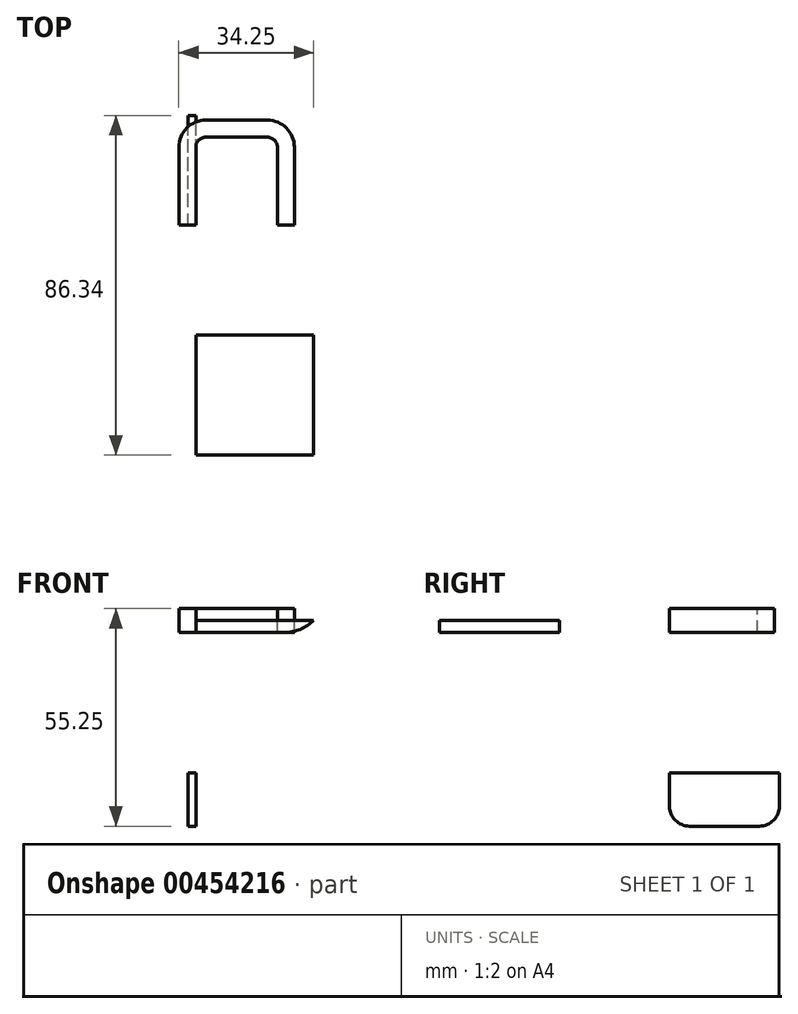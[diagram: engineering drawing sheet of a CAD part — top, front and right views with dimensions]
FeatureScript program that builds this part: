
annotation { "Feature Type Name" : "Feature", "Feature Type Description" : "" }
export const myFeature = defineFeature(function(context is Context, id is Id, definition is map)
    precondition{}
    {
        {
            var Q0;
            Q0=qCreatedBy(makeId("Top.planeOp"),FACE);
            var sketch = newSketch(context, id + "F0", { "sketchPlane" : qUnion([Q0])});
            skLineSegment(sketch, "E0", {"start": v(0, 0) * mm, "end": v(0, 19.84) * mm});
            skLineSegment(sketch, "E1", {"start": v(2.54, 22.38) * mm, "end": v(18.18, 22.38) * mm});
            skLineSegment(sketch, "E2", {"start": v(20.72, 19.84) * mm, "end": v(20.72, 0) * mm});
            skPoint(sketch, "E3.visualSharp", {"position": v(0, 22.38) * mm});
            skArc(sketch, "E3.filletArc", {"start": v(2.54, 22.38) * mm, "mid": v(0.74, 21.64) * mm, "end": v(0, 19.84) * mm});
            skPoint(sketch, "E4.visualSharp", {"position": v(20.72, 22.38) * mm});
            skArc(sketch, "E4.filletArc", {"start": v(20.72, 19.84) * mm, "mid": v(19.98, 21.64) * mm, "end": v(18.18, 22.38) * mm});
            skSolve(sketch);
        }
        {
            var Q0;
            Q0=qCreatedBy(makeId("Front.planeOp"),FACE);
            var sketch = newSketch(context, id + "F1", { "sketchPlane" : qUnion([Q0])});
            skLineSegment(sketch, "E5.bottom", {"start": v(0, 0) * mm, "end": v(-4.32, 0) * mm});
            skLineSegment(sketch, "E5.top", {"start": v(0, 6.04) * mm, "end": v(-4.32, 6.04) * mm});
            skLineSegment(sketch, "E5.left", {"start": v(0, 0) * mm, "end": v(0, 6.04) * mm});
            skLineSegment(sketch, "E5.right", {"start": v(-4.32, 0) * mm, "end": v(-4.32, 6.04) * mm});
            skSolve(sketch);
        }
        {
            var Q0;
            Q0=makeQuery(id+"F1.imprint","IMPRINT",FACE,{"disambiguationData":[TD([[makeQuery(id+"F1.imprint","IMPRINT",EDGE,{"derivedFrom":sQuery(id+"F1.wireOp",EDGE,"E5.bottom")}),-1.0]])]});
            var Q1;
            Q1=sQuery(id+"F0.wireOp",EDGE,"E0");
            var Q2;
            Q2=sQuery(id+"F0.wireOp",EDGE,"E3.filletArc");
            var Q3;
            Q3=sQuery(id+"F0.wireOp",EDGE,"E1");
            var Q4;
            Q4=sQuery(id+"F0.wireOp",EDGE,"E4.filletArc");
            var Q5;
            Q5=sQuery(id+"F0.wireOp",EDGE,"E2");
            sweep(context, id + "F2", {"profiles" : qUnion([Q0]), "path" : qUnion([Q1, Q2, Q3, Q4, Q5])});
        }
        {
            var Q0;
            Q0=qCreatedBy(makeId("Top.planeOp"),FACE);
            var sketch = newSketch(context, id + "F3", { "sketchPlane" : qUnion([Q0])});
            skLineSegment(sketch, "E6.bottom", {"start": v(0, -27.92) * mm, "end": v(29.93, -27.92) * mm});
            skLineSegment(sketch, "E6.top", {"start": v(0, -58.42) * mm, "end": v(29.93, -58.42) * mm});
            skLineSegment(sketch, "E6.left", {"start": v(0, -27.92) * mm, "end": v(0, -58.42) * mm});
            skLineSegment(sketch, "E6.right", {"start": v(29.93, -27.92) * mm, "end": v(29.93, -58.42) * mm});
            skSolve(sketch);
        }
        {
            var Q0;
            Q0=makeQuery(id+"F3.imprint","IMPRINT",FACE,{"disambiguationData":[TD([[makeQuery(id+"F3.imprint","IMPRINT",EDGE,{"derivedFrom":sQuery(id+"F3.wireOp",EDGE,"E6.bottom")}),-1.0]])]});
            extrude(context, id + "F4", {"entities" : qUnion([Q0]), "depth" : 3.05 * mm});
        }
        {
            var Q0;
            Q0=makeQuery(id+"F4.opExtrude","CAP_EDGE",EDGE,{"disambiguationData":[OSD([sQuery(id+"F3.wireOp",EDGE,"E6.right")])],"isStart":true});
            fillet(context, id + "F5", {"entities" : qUnion([Q0]), "radius" : 10.42 * mm, "tangentPropagation" : true, "allowEdgeOverflow" : false});
        }
        {
            var Q0;
            Q0=qCreatedBy(makeId("Right.planeOp"),FACE);
            var sketch = newSketch(context, id + "F6", { "sketchPlane" : qUnion([Q0])});
            skLineSegment(sketch, "E7.bottom", {"start": v(5.08, -49.21) * mm, "end": v(22.84, -49.21) * mm});
            skLineSegment(sketch, "E7.top", {"start": v(0, -35.69) * mm, "end": v(27.92, -35.69) * mm});
            skLineSegment(sketch, "E7.left", {"start": v(0, -44.13) * mm, "end": v(0, -35.69) * mm});
            skLineSegment(sketch, "E7.right", {"start": v(27.92, -44.13) * mm, "end": v(27.92, -35.69) * mm});
            skPoint(sketch, "E8.visualSharp", {"position": v(0, -49.21) * mm});
            skArc(sketch, "E8.filletArc", {"start": v(0, -44.13) * mm, "mid": v(1.49, -47.73) * mm, "end": v(5.08, -49.21) * mm});
            skPoint(sketch, "E9.visualSharp", {"position": v(27.92, -49.21) * mm});
            skArc(sketch, "E9.filletArc", {"start": v(22.84, -49.21) * mm, "mid": v(26.43, -47.73) * mm, "end": v(27.92, -44.13) * mm});
            skSolve(sketch);
        }
        {
            var Q0;
            Q0=makeQuery(id+"F6.imprint","IMPRINT",FACE,{"disambiguationData":[TD([[makeQuery(id+"F6.imprint","IMPRINT",EDGE,{"derivedFrom":sQuery(id+"F6.wireOp",EDGE,"E7.bottom")}),1.0]])]});
            extrude(context, id + "F7", {"entities" : qUnion([Q0]), "oppositeDirection" : true, "depth" : 2.03 * mm});
        }
    });
